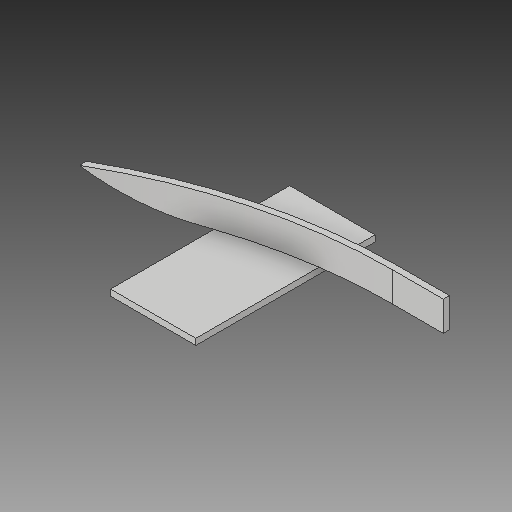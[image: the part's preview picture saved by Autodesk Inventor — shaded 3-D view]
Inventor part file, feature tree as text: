
AUTODESK INVENTOR PART (.ipt)
format: ipt  version: 2018.3 (Build 223284000, 284)  size: 151,552 bytes
history: native  units: mm
features: other x3, projected_geometry x3, extrude x2, sketch x2
ambient origin geometry x8: Origin, YZ Plane, XZ Plane, XY Plane, X Axis, Y Axis, Z Axis, Center Point
bodies: Body1 (feature_tree)
feature tree (10):
  other  "endplate_ver2.ipt"
  extrude  "押し出し1"  Depth=10.0mm
  extrude  "押し出し2"  Depth=10.0mm TaperAngle=0.0deg
  other  "ソリッド2::endplate_ver2.ipt"
  other  "TaggingFeature1"
  sketch  "スケッチ1"
  projected_geometry  "投影ループ1"
  projected_geometry  "投影ループ2"
  sketch  "スケッチ2"
  projected_geometry  "投影ループ3"
